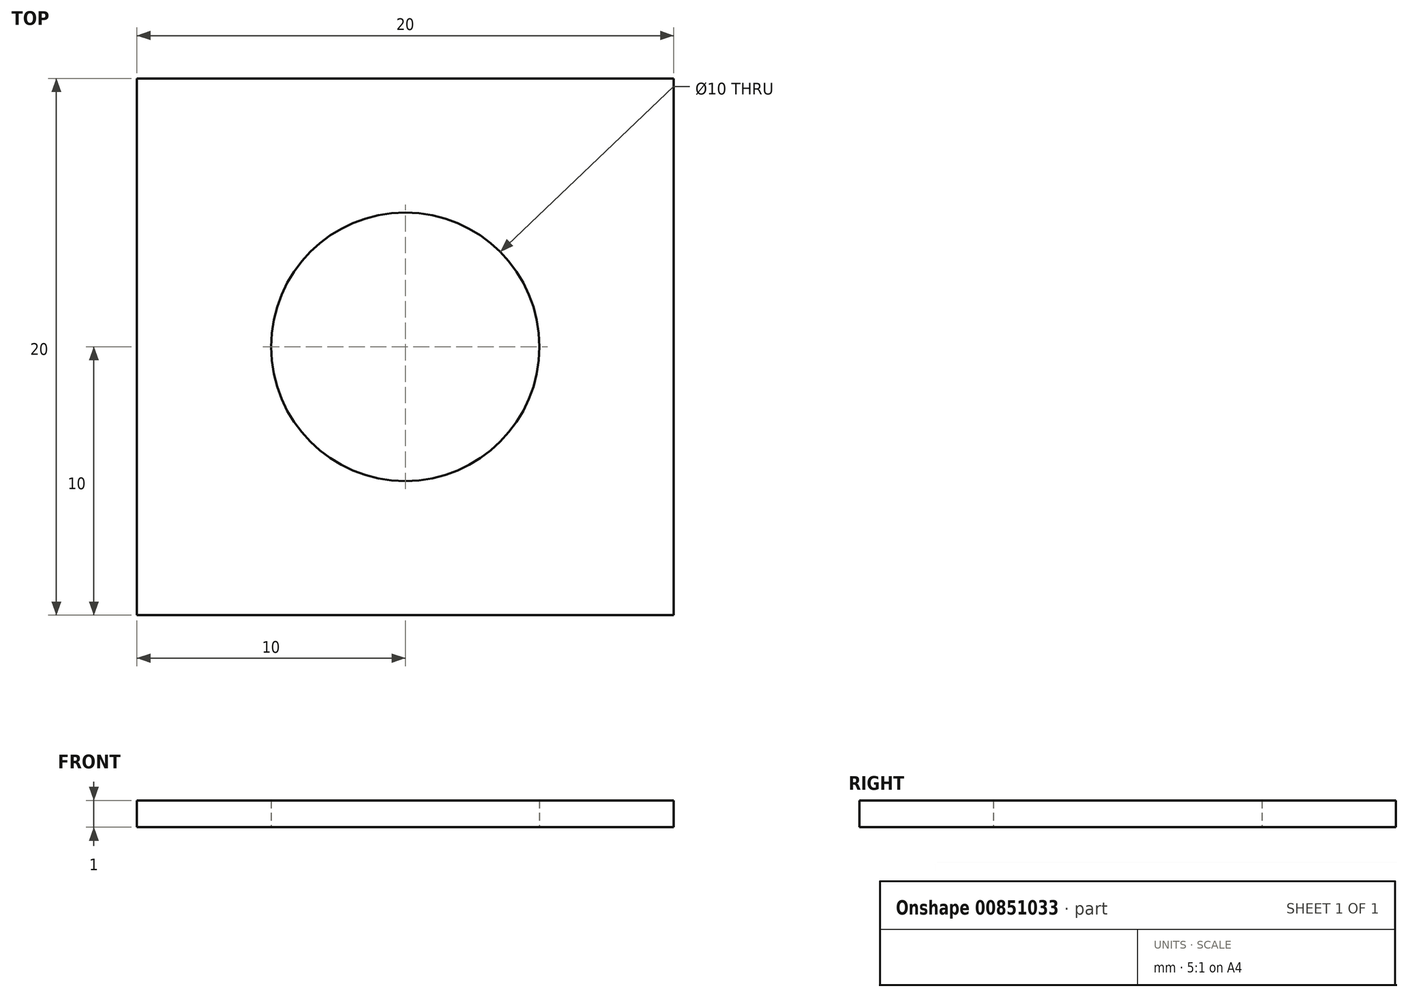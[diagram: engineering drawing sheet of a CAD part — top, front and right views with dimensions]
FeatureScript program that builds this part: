
annotation { "Feature Type Name" : "Feature", "Feature Type Description" : "" }
export const myFeature = defineFeature(function(context is Context, id is Id, definition is map)
    precondition{}
    {
        {
            var Q0;
            Q0=qCreatedBy(makeId("Top.planeOp"),FACE);
            var sketch = newSketch(context, id + "F0", { "sketchPlane" : qUnion([Q0])});
            skLineSegment(sketch, "E0.bottom", {"start": v(10, -10) * mm, "end": v(-10, -10) * mm});
            skLineSegment(sketch, "E0.top", {"start": v(10, 10) * mm, "end": v(-10, 10) * mm});
            skLineSegment(sketch, "E0.left", {"start": v(10, -10) * mm, "end": v(10, 10) * mm});
            skLineSegment(sketch, "E0.right", {"start": v(-10, -10) * mm, "end": v(-10, 10) * mm});
            skPoint(sketch, "E0.middle", {"position": v(0, 0) * mm});
            skCircle(sketch, "E1", {"center": v(0, 0) * mm, "radius": 5 * mm});
            skSolve(sketch);
        }
        {
            var Q0;
            Q0=makeQuery(id+"F0.imprint","IMPRINT",FACE,{"disambiguationData":[TD([[makeQuery(id+"F0.imprint","IMPRINT",EDGE,{"derivedFrom":sQuery(id+"F0.wireOp",EDGE,"E0.bottom")}),-1.0]])]});
            extrude(context, id + "F1", {"entities" : qUnion([Q0]), "endBound" : BoundingType.SYMMETRIC, "depth" : 1 * mm, "offsetDistance" : 25 * mm});
        }
    });
